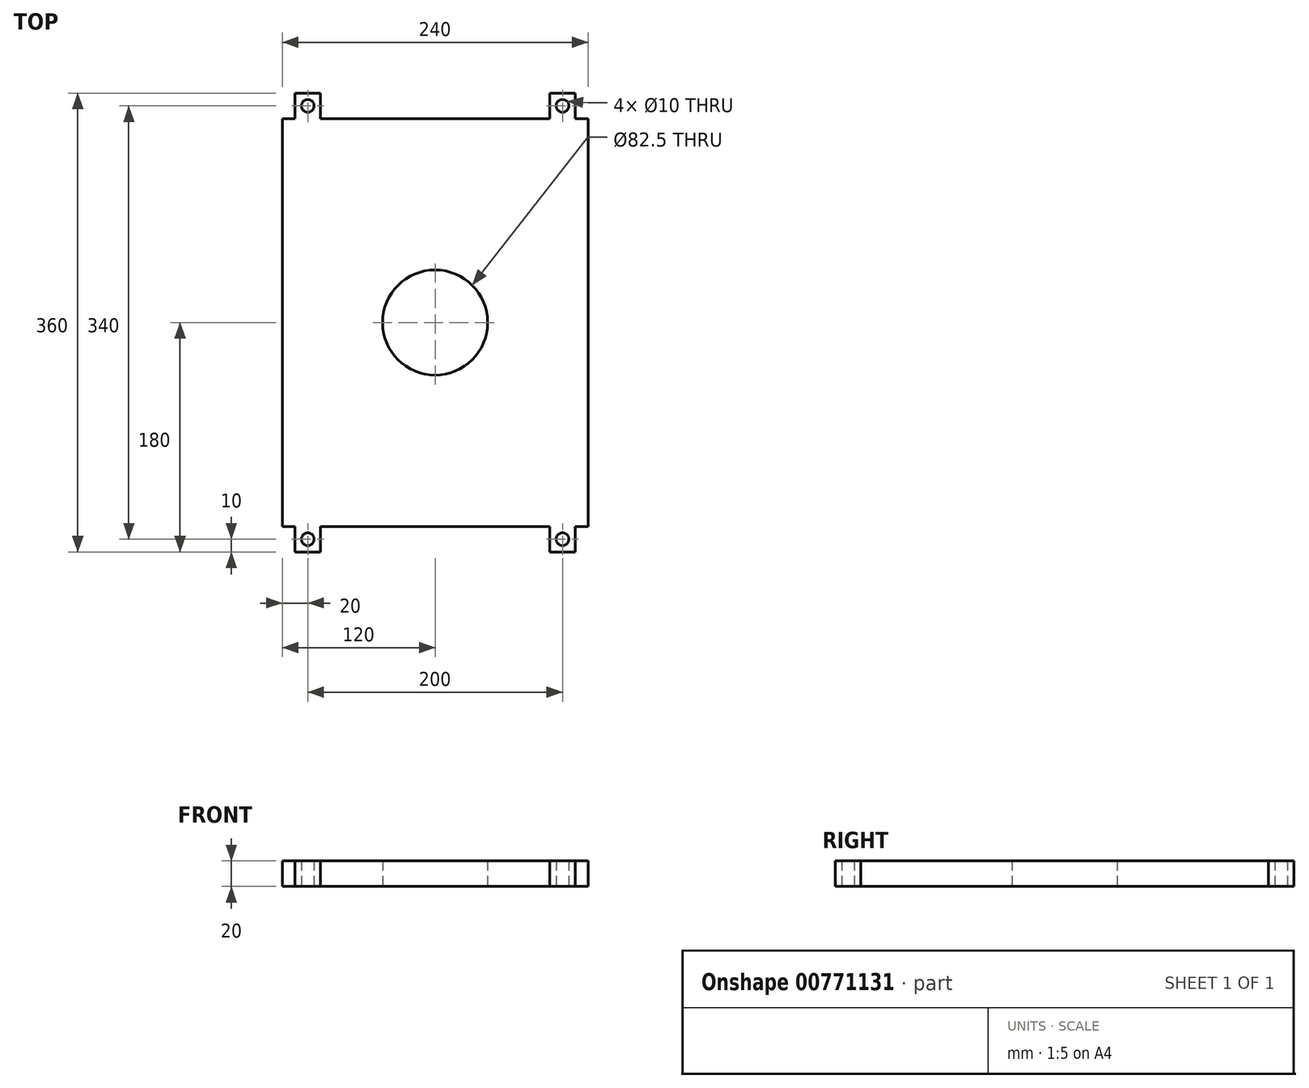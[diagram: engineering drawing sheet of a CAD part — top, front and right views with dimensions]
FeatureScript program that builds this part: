
annotation { "Feature Type Name" : "Feature", "Feature Type Description" : "" }
export const myFeature = defineFeature(function(context is Context, id is Id, definition is map)
    precondition{}
    {
        {
            var Q0;
            Q0=qCreatedBy(makeId("Top.planeOp"),FACE);
            var sketch = newSketch(context, id + "F0", { "sketchPlane" : qUnion([Q0])});
            skLineSegment(sketch, "E0.bottom", {"start": v(120, -160) * mm, "end": v(-120, -160) * mm});
            skLineSegment(sketch, "E0.top", {"start": v(120, 160) * mm, "end": v(-120, 160) * mm});
            skLineSegment(sketch, "E0.left", {"start": v(120, -160) * mm, "end": v(120, 160) * mm});
            skLineSegment(sketch, "E0.right", {"start": v(-120, -160) * mm, "end": v(-120, 160) * mm});
            skPoint(sketch, "E0.middle", {"position": v(0, 0) * mm});
            skCircle(sketch, "E1", {"center": v(0, 0) * mm, "radius": 41.25 * mm});
            skLineSegment(sketch, "E2.bottom", {"start": v(-110, 160) * mm, "end": v(-90, 160) * mm});
            skLineSegment(sketch, "E2.top", {"start": v(-110, 180) * mm, "end": v(-90, 180) * mm});
            skLineSegment(sketch, "E2.left", {"start": v(-110, 160) * mm, "end": v(-110, 180) * mm});
            skLineSegment(sketch, "E2.right", {"start": v(-90, 160) * mm, "end": v(-90, 180) * mm});
            skCircle(sketch, "E3", {"center": v(-100, 170) * mm, "radius": 5 * mm});
            skPoint(sketch, "E3.centerSnap0", {"position": v(-100, 180) * mm});
            skPoint(sketch, "E3.centerSnap1", {"position": v(-110, 170) * mm});
            skLineSegment(sketch, "E4.MirrorCS", {"start": v(110, 160) * mm, "end": v(110, 180) * mm});
            skPoint(sketch, "E5.MirrorP", {"position": v(100, 180) * mm});
            skLineSegment(sketch, "E6.MirrorCS", {"start": v(110, 180) * mm, "end": v(90, 180) * mm});
            skPoint(sketch, "E7.MirrorP", {"position": v(110, 170) * mm});
            skLineSegment(sketch, "E8.MirrorCS", {"start": v(90, 160) * mm, "end": v(90, 180) * mm});
            skCircle(sketch, "E9.MirrorC", {"center": v(100, 170) * mm, "radius": 5 * mm});
            skCircle(sketch, "E10.MirrorC", {"center": v(100, -170) * mm, "radius": 5 * mm});
            skLineSegment(sketch, "E11.MirrorCS", {"start": v(110, -180) * mm, "end": v(90, -180) * mm});
            skLineSegment(sketch, "E12.MirrorCS", {"start": v(-110, -160) * mm, "end": v(-110, -180) * mm});
            skLineSegment(sketch, "E13.MirrorCS", {"start": v(-110, -180) * mm, "end": v(-90, -180) * mm});
            skLineSegment(sketch, "E14.MirrorCS", {"start": v(110, -160) * mm, "end": v(110, -180) * mm});
            skCircle(sketch, "E15.MirrorC", {"center": v(-100, -170) * mm, "radius": 5 * mm});
            skPoint(sketch, "E16.MirrorP", {"position": v(-110, -170) * mm});
            skPoint(sketch, "E17.MirrorP", {"position": v(110, -170) * mm});
            skPoint(sketch, "E18.MirrorP", {"position": v(-100, -180) * mm});
            skLineSegment(sketch, "E19.MirrorCS", {"start": v(90, -160) * mm, "end": v(90, -180) * mm});
            skPoint(sketch, "E20.MirrorP", {"position": v(100, -180) * mm});
            skLineSegment(sketch, "E21.MirrorCS", {"start": v(-90, -160) * mm, "end": v(-90, -180) * mm});
            skSolve(sketch);
        }
        {
            var Q0;
            {var subQ3=sQuery(id+"F0.wireOp",EDGE,"E4.MirrorCS");var subQ6=sQuery(id+"F0.wireOp",EDGE,"E12.MirrorCS");var subQ23=sQuery(id+"F0.wireOp",EDGE,"E0.left");Q0=qUnion([makeQuery(id+"F0.imprint","IMPRINT",FACE,{"disambiguationData":[TD([[makeQuery(id+"F0.imprint","IMPRINT",EDGE,{"derivedFrom":subQ23}),1.0]])]}),makeQuery(id+"F0.imprint","IMPRINT",FACE,{"disambiguationData":[TD([[makeQuery(id+"F0.imprint","IMPRINT",EDGE,{"derivedFrom":sQuery(id+"F0.wireOp",EDGE,"E10.MirrorC")}),-1.0]])]}),makeQuery(id+"F0.imprint","IMPRINT",FACE,{"disambiguationData":[TD([[makeQuery(id+"F0.imprint","IMPRINT",EDGE,{"derivedFrom":sQuery(id+"F0.wireOp",EDGE,"E2.top")}),-1.0]])]}),makeQuery(id+"F0.imprint","IMPRINT",FACE,{"disambiguationData":[TD([[makeQuery(id+"F0.imprint","IMPRINT",EDGE,{"derivedFrom":subQ6}),1.0]])]}),makeQuery(id+"F0.imprint","IMPRINT",FACE,{"disambiguationData":[TD([[makeQuery(id+"F0.imprint","IMPRINT",EDGE,{"derivedFrom":subQ3}),1.0]])]})]);}
            extrude(context, id + "F1", {"entities" : qUnion([Q0]), "depth" : 20 * mm, "offsetDistance" : 25 * mm});
        }
    });
